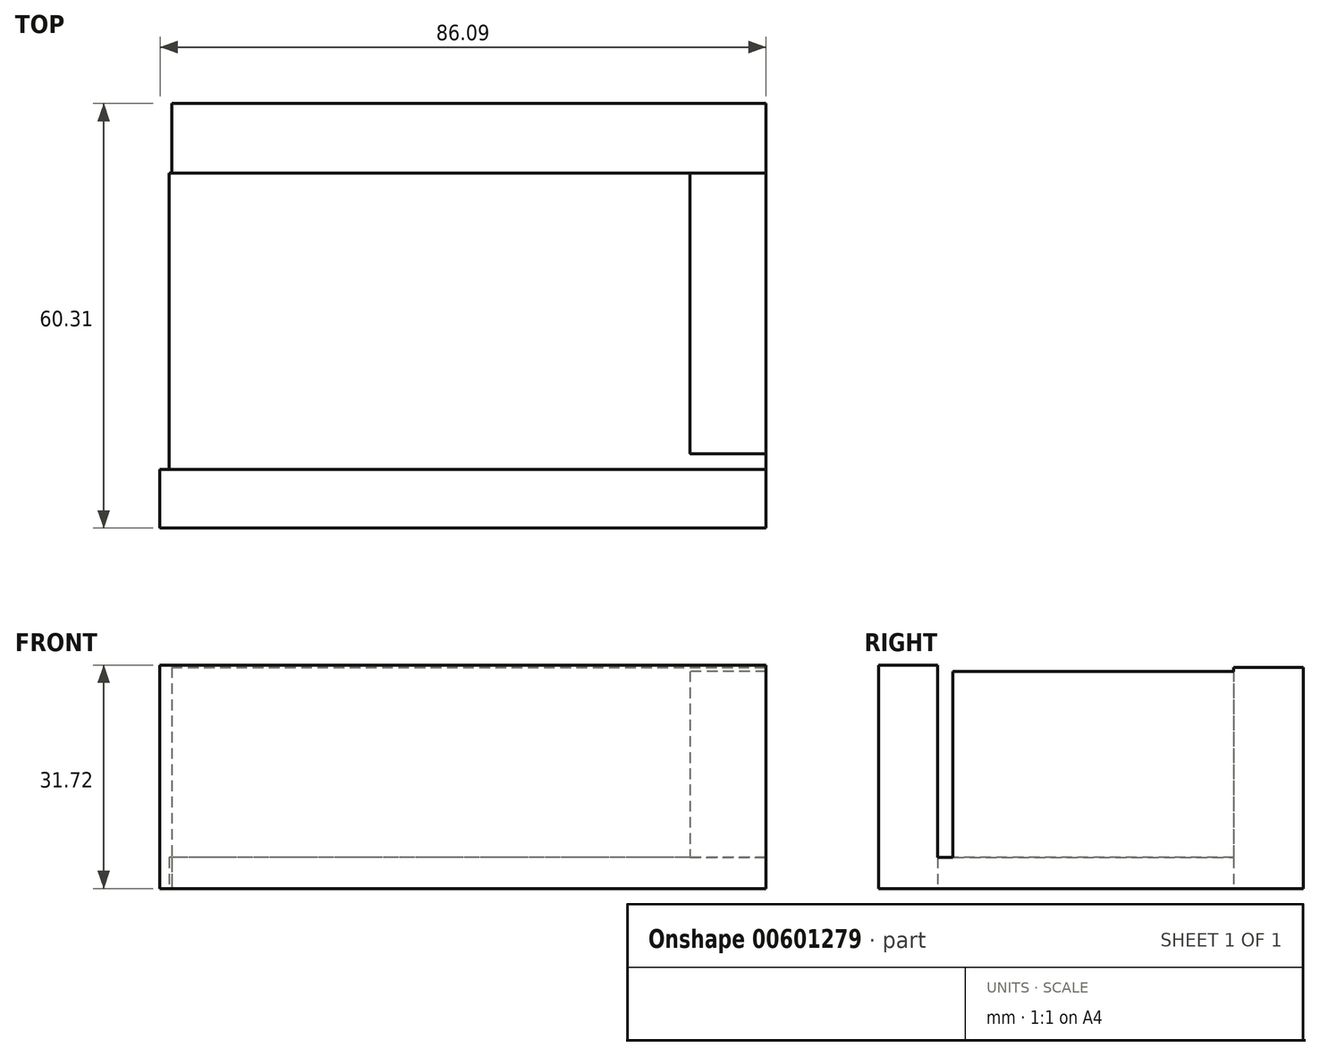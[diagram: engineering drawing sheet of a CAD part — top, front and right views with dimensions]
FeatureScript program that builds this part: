
annotation { "Feature Type Name" : "Feature", "Feature Type Description" : "" }
export const myFeature = defineFeature(function(context is Context, id is Id, definition is map)
    precondition{}
    {
        {
            var Q0;
            Q0=qCreatedBy(makeId("Top.planeOp"),FACE);
            var sketch = newSketch(context, id + "F0", { "sketchPlane" : qUnion([Q0])});
            skLineSegment(sketch, "E0.bottom", {"start": v(0, -43.27) * mm, "end": v(-84.78, -43.27) * mm});
            skLineSegment(sketch, "E0.top", {"start": v(0, 0) * mm, "end": v(-84.78, 0) * mm});
            skLineSegment(sketch, "E0.left", {"start": v(0, -43.27) * mm, "end": v(0, 0) * mm});
            skLineSegment(sketch, "E0.right", {"start": v(-84.78, -43.27) * mm, "end": v(-84.78, 0) * mm});
            skSolve(sketch);
        }
        {
            var Q0;
            Q0 = qSketchRegion(id + "F0", true);
            extrude(context, id + "F1", {"entities" : qUnion([Q0]), "depth" : 4.4 * mm, "offsetDistance" : 25.4 * mm});
        }
        {
            var Q0;
            Q0=qCreatedBy(makeId("Top.planeOp"),FACE);
            var sketch = newSketch(context, id + "F2", { "sketchPlane" : qUnion([Q0])});
            skLineSegment(sketch, "E1.bottom", {"start": v(-84.42, 0) * mm, "end": v(0, 0) * mm});
            skLineSegment(sketch, "E1.top", {"start": v(-84.42, 9.88) * mm, "end": v(0, 9.88) * mm});
            skLineSegment(sketch, "E1.left", {"start": v(-84.42, 0) * mm, "end": v(-84.42, 9.88) * mm});
            skLineSegment(sketch, "E1.right", {"start": v(0, 0) * mm, "end": v(0, 9.88) * mm});
            skSolve(sketch);
        }
        {
            var Q0;
            Q0 = qSketchRegion(id + "F2", true);
            var Q1;
            Q1 = qSketchRegion(id + "F2", true);
            extrude(context, id + "F3", {"entities" : qUnion([Q0, Q1]), "operationType" : NewBodyOperationType.ADD, "depth" : 31.43 * mm, "offsetDistance" : 25.4 * mm});
        }
        {
            var Q0;
            Q0=qCreatedBy(makeId("Top.planeOp"),FACE);
            var sketch = newSketch(context, id + "F4", { "sketchPlane" : qUnion([Q0])});
            skLineSegment(sketch, "E2.bottom", {"start": v(-86.1, -42.09) * mm, "end": v(0, -42.09) * mm});
            skLineSegment(sketch, "E2.top", {"start": v(-86.1, -50.43) * mm, "end": v(0, -50.43) * mm});
            skLineSegment(sketch, "E2.left", {"start": v(-86.1, -42.09) * mm, "end": v(-86.1, -50.43) * mm});
            skLineSegment(sketch, "E2.right", {"start": v(0, -42.09) * mm, "end": v(0, -50.43) * mm});
            skSolve(sketch);
        }
        {
            var Q0;
            Q0 = qSketchRegion(id + "F4", true);
            extrude(context, id + "F5", {"entities" : qUnion([Q0]), "operationType" : NewBodyOperationType.ADD, "depth" : 31.72 * mm, "offsetDistance" : 25.4 * mm});
        }
        {
            var Q0;
            Q0=qCreatedBy(makeId("Top.planeOp"),FACE);
            var sketch = newSketch(context, id + "F6", { "sketchPlane" : qUnion([Q0])});
            skLineSegment(sketch, "E3.bottom", {"start": v(0, -39.9) * mm, "end": v(-10.8, -39.9) * mm});
            skLineSegment(sketch, "E3.top", {"start": v(0, 0) * mm, "end": v(-10.8, 0) * mm});
            skLineSegment(sketch, "E3.left", {"start": v(0, -39.9) * mm, "end": v(0, 0) * mm});
            skLineSegment(sketch, "E3.right", {"start": v(-10.8, -39.9) * mm, "end": v(-10.8, 0) * mm});
            skSolve(sketch);
        }
        {
            var Q0;
            Q0 = qSketchRegion(id + "F6", true);
            extrude(context, id + "F7", {"entities" : qUnion([Q0]), "operationType" : NewBodyOperationType.ADD, "depth" : 30.85 * mm, "offsetDistance" : 25.4 * mm});
        }
    });
